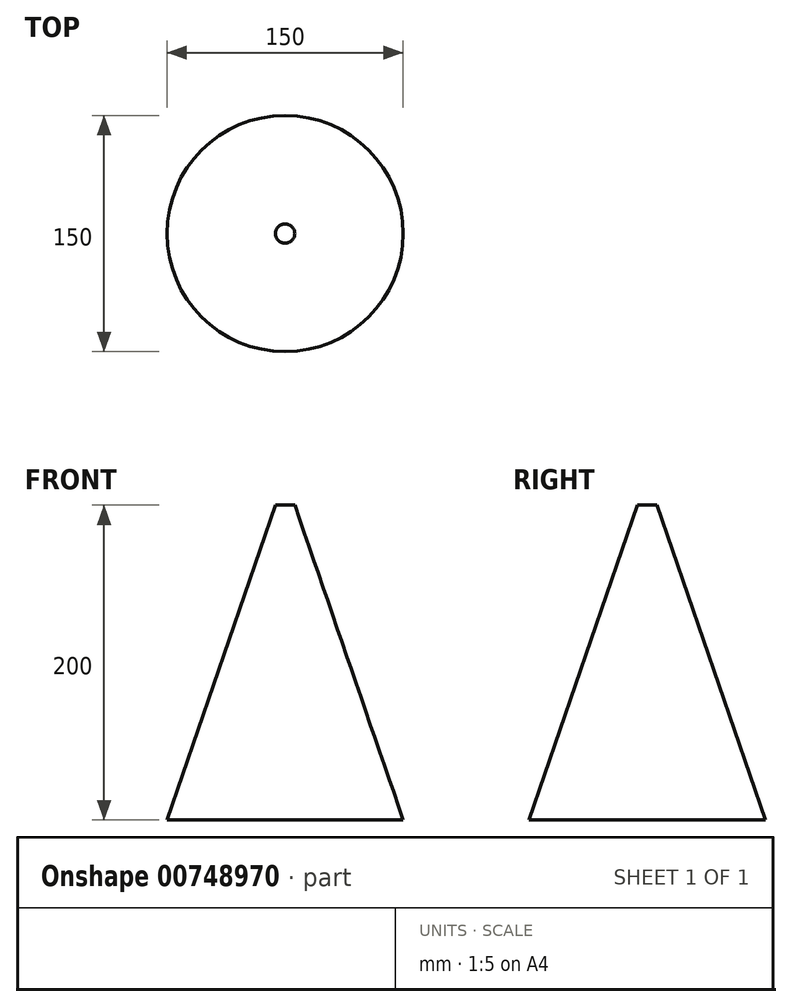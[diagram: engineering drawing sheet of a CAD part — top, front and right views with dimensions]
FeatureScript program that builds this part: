
annotation { "Feature Type Name" : "Feature", "Feature Type Description" : "" }
export const myFeature = defineFeature(function(context is Context, id is Id, definition is map)
    precondition{}
    {
        {
            var Q0;
            Q0=qCreatedBy(makeId("Top.planeOp"),FACE);
            var sketch = newSketch(context, id + "F0", { "sketchPlane" : qUnion([Q0])});
            skCircle(sketch, "E0", {"center": v(0, 0) * mm, "radius": 75 * mm});
            skSolve(sketch);
        }
        {
            var Q0;
            Q0=makeQuery(id+"F0.imprint","IMPRINT",FACE,{"disambiguationData":[TD([[makeQuery(id+"F0.imprint","IMPRINT",EDGE,{"derivedFrom":sQuery(id+"F0.wireOp",EDGE,"E0")}),1.0]])]});
            extrude(context, id + "F1", {"entities" : qUnion([Q0]), "depth" : 200 * mm, "offsetDistance" : 25 * mm, "hasDraft" : true, "draftAngle" : 19 * degree, "draftPullDirection" : true});
        }
    });
